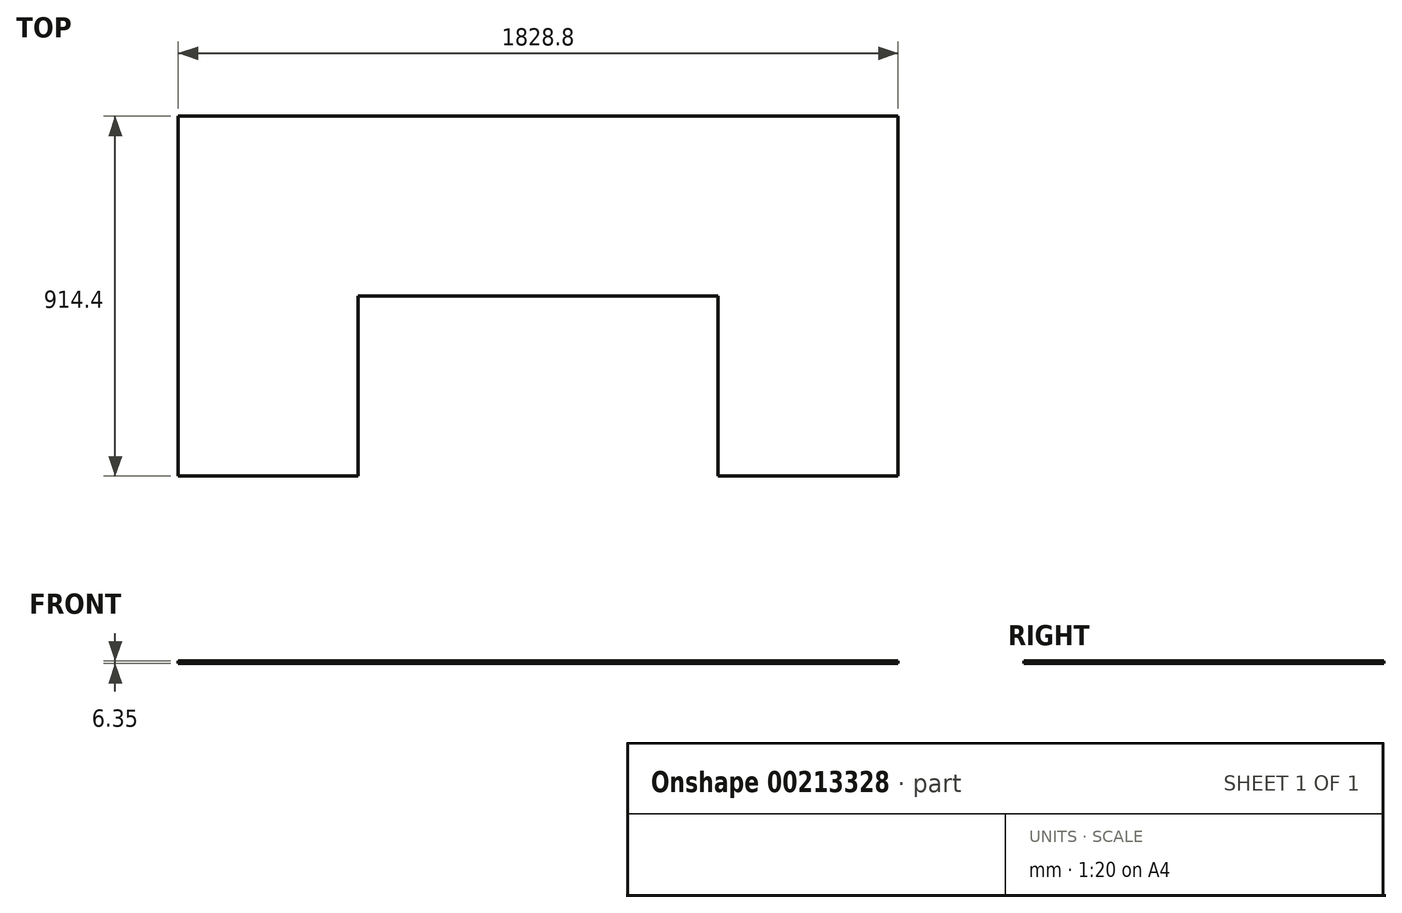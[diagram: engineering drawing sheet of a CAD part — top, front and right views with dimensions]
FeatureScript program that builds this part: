
annotation { "Feature Type Name" : "Feature", "Feature Type Description" : "" }
export const myFeature = defineFeature(function(context is Context, id is Id, definition is map)
    precondition{}
    {
        {
            var Q0;
            Q0=qCreatedBy(makeId("Top.planeOp"),FACE);
            var sketch = newSketch(context, id + "F0", { "sketchPlane" : qUnion([Q0])});
            skLineSegment(sketch, "E0.bottom", {"start": v(914.4, 457.2) * mm, "end": v(-914.4, 457.2) * mm});
            skLineSegment(sketch, "E0.top", {"start": v(914.4, -457.2) * mm, "end": v(457.2, -457.2) * mm});
            skLineSegment(sketch, "E0.left", {"start": v(914.4, 457.2) * mm, "end": v(914.4, -457.2) * mm});
            skLineSegment(sketch, "E0.right", {"start": v(-914.4, 457.2) * mm, "end": v(-914.4, -457.2) * mm});
            skPoint(sketch, "E0.middle", {"position": v(0, 0) * mm});
            skLineSegment(sketch, "E1", {"start": v(-457.2, -457.2) * mm, "end": v(-457.2, 0) * mm});
            skLineSegment(sketch, "E2", {"start": v(-457.2, 0) * mm, "end": v(457.2, 0) * mm});
            skLineSegment(sketch, "E3", {"start": v(457.2, 0) * mm, "end": v(457.2, -457.2) * mm});
            skLineSegment(sketch, "E4.trimOffspring", {"start": v(-457.2, -457.2) * mm, "end": v(-914.4, -457.2) * mm});
            skSolve(sketch);
        }
        {
            var Q0;
            Q0 = qSketchRegion(id + "F0", true);
            extrude(context, id + "F1", {"entities" : qUnion([Q0]), "depth" : 6.35 * mm});
        }
    });
